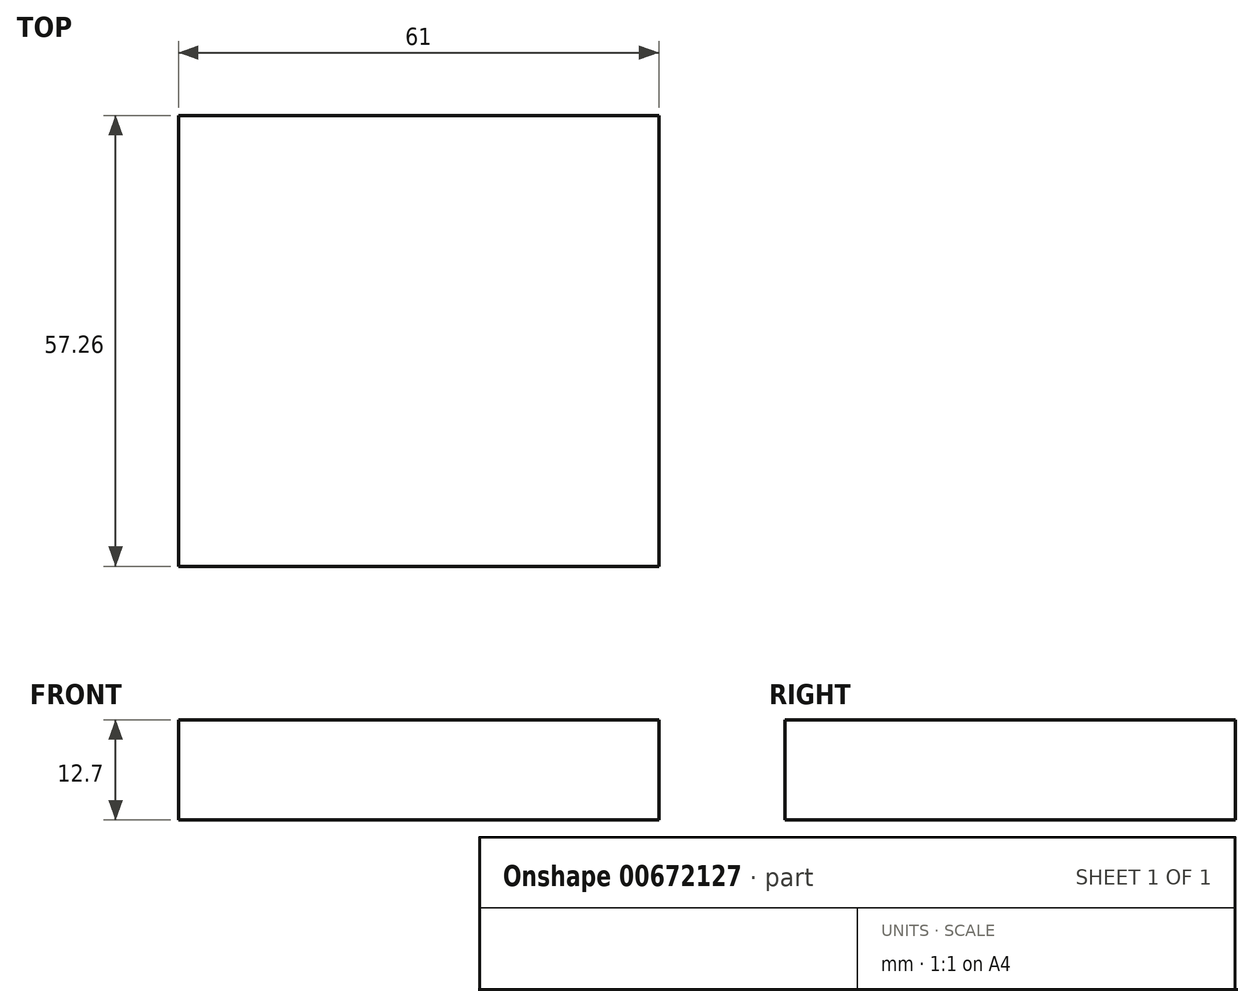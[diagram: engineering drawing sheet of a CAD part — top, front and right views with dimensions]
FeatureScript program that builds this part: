
annotation { "Feature Type Name" : "Feature", "Feature Type Description" : "" }
export const myFeature = defineFeature(function(context is Context, id is Id, definition is map)
    precondition{}
    {
        {
            var Q0;
            Q0=qCreatedBy(makeId("Top.planeOp"),FACE);
            var sketch = newSketch(context, id + "F0", { "sketchPlane" : qUnion([Q0])});
            skLineSegment(sketch, "E0.bottom", {"start": v(30.5, -28.63) * mm, "end": v(-30.5, -28.63) * mm});
            skLineSegment(sketch, "E0.top", {"start": v(30.5, 28.63) * mm, "end": v(-30.5, 28.63) * mm});
            skLineSegment(sketch, "E0.left", {"start": v(30.5, -28.63) * mm, "end": v(30.5, 28.63) * mm});
            skLineSegment(sketch, "E0.right", {"start": v(-30.5, -28.63) * mm, "end": v(-30.5, 28.63) * mm});
            skPoint(sketch, "E0.middle", {"position": v(0, 0) * mm});
            skSolve(sketch);
        }
        {
            var Q0;
            Q0=makeQuery(id+"F0.imprint","IMPRINT",FACE,{"disambiguationData":[TD([[makeQuery(id+"F0.imprint","IMPRINT",EDGE,{"derivedFrom":sQuery(id+"F0.wireOp",EDGE,"E0.bottom")}),-1.0]])]});
            extrude(context, id + "F1", {"entities" : qUnion([Q0]), "depth" : 12.7 * mm, "offsetDistance" : 25.4 * mm});
        }
    });
